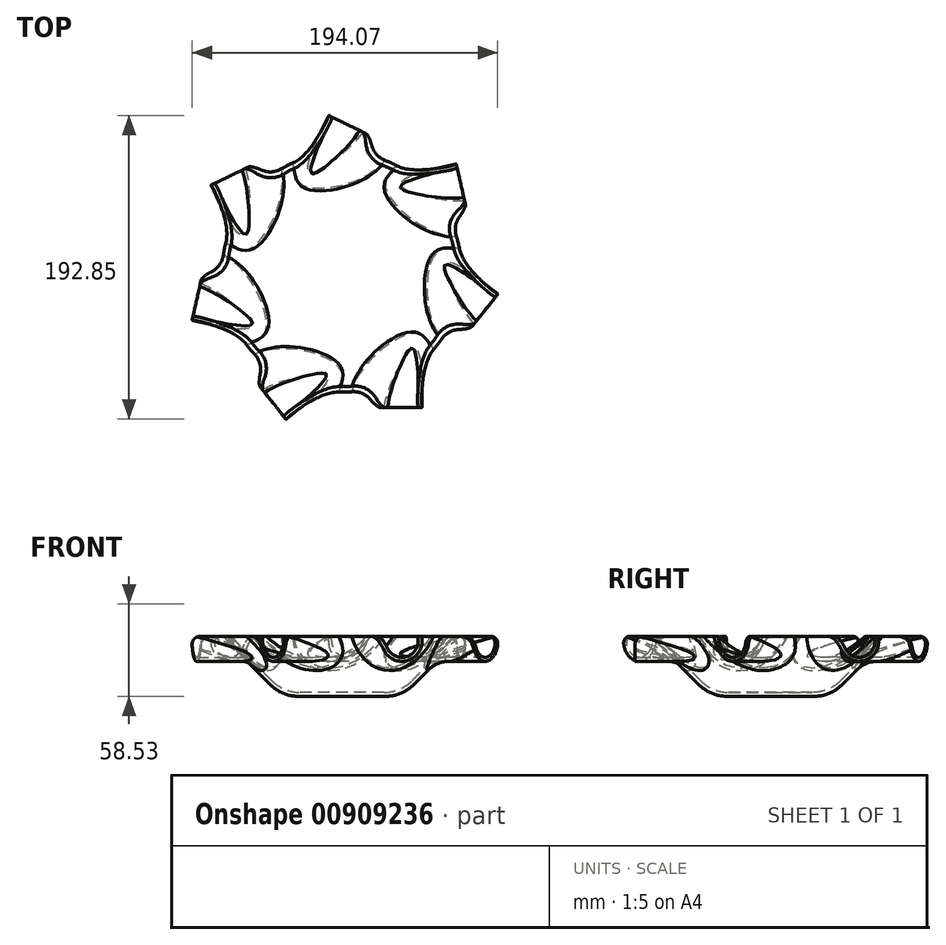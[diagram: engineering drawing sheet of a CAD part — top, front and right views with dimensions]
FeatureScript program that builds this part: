
annotation { "Feature Type Name" : "Feature", "Feature Type Description" : "" }
export const myFeature = defineFeature(function(context is Context, id is Id, definition is map)
    precondition{}
    {
        {
            var Q0;
            Q0=qCreatedBy(makeId("Front.planeOp"),FACE);
            var sketch = newSketch(context, id + "F0", { "sketchPlane" : qUnion([Q0])});
            skLineSegment(sketch, "E0", {"start": v(0, 0) * mm, "end": v(38.08, 0) * mm});
            skLineSegment(sketch, "E1", {"start": v(38.08, 0) * mm, "end": v(76.15, 38.08) * mm});
            skLineSegment(sketch, "E2", {"start": v(76.15, 38.08) * mm, "end": v(0, 38.08) * mm});
            skLineSegment(sketch, "E3", {"start": v(0, 38.08) * mm, "end": v(0, 0) * mm});
            skSolve(sketch);
        }
        {
            var Q0;
            Q0=makeQuery(id+"F0.imprint","IMPRINT",FACE,{"disambiguationData":[TD([[makeQuery(id+"F0.imprint","IMPRINT",EDGE,{"derivedFrom":sQuery(id+"F0.wireOp",EDGE,"E0")}),1.0]])]});
            var Q1;
            Q1=sQuery(id+"F0.wireOp",EDGE,"E3");
            revolve(context, id + "F1", {"surfaceOperationType" : NewSurfaceOperationType.NEW, "entities" : qUnion([Q0]), "axis" : qUnion([Q1]), "revolveType" : RevolveType.FULL});
        }
        {
            var Q0;
            Q0=qCreatedBy(makeId("Front.planeOp"),FACE);
            var sketch = newSketch(context, id + "F2", { "sketchPlane" : qUnion([Q0])});
            skLineSegment(sketch, "E4.0", {"start": v(-76.15, 38.08) * mm, "end": v(76.15, 38.08) * mm});
            skLineSegment(sketch, "E5", {"start": v(76.15, 38.08) * mm, "end": v(38.08, 0) * mm});
            skLineSegment(sketch, "E6", {"start": v(-38.08, 0) * mm, "end": v(-76.15, 38.08) * mm});
            skLineSegment(sketch, "E7.0", {"start": v(-38.08, 0) * mm, "end": v(38.08, 0) * mm});
            skCircle(sketch, "E8", {"center": v(38.08, 35) * mm, "radius": 12.76 * mm});
            skSolve(sketch);
        }
        {
            var Q0;
            {var subQ0=sQuery(id+"F2.wireOp",EDGE,"E8");var subQ1=sQuery(id+"F2.wireOp",EDGE,"E4.0");var subQ2=makeQuery(id+"F2.imprint","INTERSECT",VERTEX,{"disambiguationData":[OD(0.0)],"derivedFrom":[subQ1,subQ0]});Q0=makeQuery(id+"F2.imprint","IMPRINT",FACE,{"disambiguationData":[TD([[makeQuery(id+"F2.imprint","IMPRINT",EDGE,{"disambiguationData":[TD([[subQ2,-1.0]])],"derivedFrom":subQ1}),-1.0]])]});}
            extrude(context, id + "F3", {"entities" : qUnion([Q0]), "depth" : 86.04 * mm, "offsetDistance" : 25 * mm});
        }
        {
            var Q0;
            Q0=makeQuery(id+"F3.opExtrude","SWEPT_BODY",BODY,{"disambiguationData":[OSD([sQuery(id+"F2.wireOp",EDGE,"E4.0"),sQuery(id+"F2.wireOp",EDGE,"E8")])]});
            var Q1;
            Q1=makeQuery(id+"F1.opRevolve","SWEPT_FACE",FACE,{"disambiguationData":[OSD([sQuery(id+"F0.wireOp",EDGE,"E1")])]});
            circularPattern(context, id + "F4", {"operationType" : NewBodyOperationType.ADD, "entities" : qUnion([Q0]), "axis" : qUnion([Q1]), "angle" : 360 * degree, "instanceCount" : 7, "equalSpace" : true});
        }
        {
            var Q0;
            Q0=makeQuery(id+"F4.boolean.opBoolean","INTERSECT",EDGE,{"derivedFrom":[makeQuery(id+"F1.opRevolve","SWEPT_FACE",FACE,{"disambiguationData":[OSD([sQuery(id+"F0.wireOp",EDGE,"E1")])]}),makeQuery(id+"F4.opPattern","COPY",FACE,{"derivedFrom":makeQuery(id+"F3.opExtrude","SWEPT_FACE",FACE,{"disambiguationData":[OSD([sQuery(id+"F2.wireOp",EDGE,"E8")])]}),"instanceName":"6"})]});
            var Q1;
            Q1=makeQuery(id+"F4.boolean.opBoolean","INTERSECT",EDGE,{"derivedFrom":[makeQuery(id+"F1.opRevolve","SWEPT_FACE",FACE,{"disambiguationData":[OSD([sQuery(id+"F0.wireOp",EDGE,"E1")])]}),makeQuery(id+"F3.opExtrude","SWEPT_FACE",FACE,{"disambiguationData":[OSD([sQuery(id+"F2.wireOp",EDGE,"E8")])]})]});
            var Q2;
            Q2=makeQuery(id+"F4.boolean.opBoolean","INTERSECT",EDGE,{"derivedFrom":[makeQuery(id+"F1.opRevolve","SWEPT_FACE",FACE,{"disambiguationData":[OSD([sQuery(id+"F0.wireOp",EDGE,"E1")])]}),makeQuery(id+"F4.opPattern","COPY",FACE,{"derivedFrom":makeQuery(id+"F3.opExtrude","SWEPT_FACE",FACE,{"disambiguationData":[OSD([sQuery(id+"F2.wireOp",EDGE,"E8")])]}),"instanceName":"1"})]});
            var Q3;
            Q3=makeQuery(id+"F4.boolean.opBoolean","INTERSECT",EDGE,{"derivedFrom":[makeQuery(id+"F1.opRevolve","SWEPT_FACE",FACE,{"disambiguationData":[OSD([sQuery(id+"F0.wireOp",EDGE,"E1")])]}),makeQuery(id+"F4.opPattern","COPY",FACE,{"derivedFrom":makeQuery(id+"F3.opExtrude","SWEPT_FACE",FACE,{"disambiguationData":[OSD([sQuery(id+"F2.wireOp",EDGE,"E8")])]}),"instanceName":"5"})]});
            var Q4;
            Q4=makeQuery(id+"F4.boolean.opBoolean","INTERSECT",EDGE,{"derivedFrom":[makeQuery(id+"F1.opRevolve","SWEPT_FACE",FACE,{"disambiguationData":[OSD([sQuery(id+"F0.wireOp",EDGE,"E1")])]}),makeQuery(id+"F4.opPattern","COPY",FACE,{"derivedFrom":makeQuery(id+"F3.opExtrude","SWEPT_FACE",FACE,{"disambiguationData":[OSD([sQuery(id+"F2.wireOp",EDGE,"E8")])]}),"instanceName":"4"})]});
            var Q5;
            Q5=makeQuery(id+"F4.boolean.opBoolean","INTERSECT",EDGE,{"derivedFrom":[makeQuery(id+"F1.opRevolve","SWEPT_FACE",FACE,{"disambiguationData":[OSD([sQuery(id+"F0.wireOp",EDGE,"E1")])]}),makeQuery(id+"F4.opPattern","COPY",FACE,{"derivedFrom":makeQuery(id+"F3.opExtrude","SWEPT_FACE",FACE,{"disambiguationData":[OSD([sQuery(id+"F2.wireOp",EDGE,"E8")])]}),"instanceName":"3"})]});
            var Q6;
            Q6=makeQuery(id+"F4.boolean.opBoolean","INTERSECT",EDGE,{"derivedFrom":[makeQuery(id+"F1.opRevolve","SWEPT_FACE",FACE,{"disambiguationData":[OSD([sQuery(id+"F0.wireOp",EDGE,"E1")])]}),makeQuery(id+"F4.opPattern","COPY",FACE,{"derivedFrom":makeQuery(id+"F3.opExtrude","SWEPT_FACE",FACE,{"disambiguationData":[OSD([sQuery(id+"F2.wireOp",EDGE,"E8")])]}),"instanceName":"2"})]});
            fillet(context, id + "F5", {"entities" : qUnion([Q0, Q1, Q2, Q3, Q4, Q5, Q6]), "radius" : 20 * mm, "tangentPropagation" : true, "allowEdgeOverflow" : false});
        }
        {
            var Q0;
            {var subQ0=makeQuery(id+"F3.opExtrude","SWEPT_FACE",FACE,{"disambiguationData":[OSD([sQuery(id+"F2.wireOp",EDGE,"E4.0")])]});Q0=makeQuery(id+"F4.boolean.opBoolean","MERGE",FACE,{"derivedFrom":[makeQuery(id+"F1.opRevolve","SWEPT_FACE",FACE,{"disambiguationData":[OSD([sQuery(id+"F0.wireOp",EDGE,"E2")])]}),subQ0,makeQuery(id+"F4.opPattern","COPY",FACE,{"derivedFrom":subQ0,"instanceName":"1"}),makeQuery(id+"F4.opPattern","COPY",FACE,{"derivedFrom":subQ0,"instanceName":"2"}),makeQuery(id+"F4.opPattern","COPY",FACE,{"derivedFrom":subQ0,"instanceName":"3"}),makeQuery(id+"F4.opPattern","COPY",FACE,{"derivedFrom":subQ0,"instanceName":"4"}),makeQuery(id+"F4.opPattern","COPY",FACE,{"derivedFrom":subQ0,"instanceName":"5"}),makeQuery(id+"F4.opPattern","COPY",FACE,{"derivedFrom":subQ0,"instanceName":"6"})]});}
            var Q1;
            Q1=makeQuery(id+"F4.opPattern","COPY",FACE,{"derivedFrom":makeQuery(id+"F3.opExtrude","CAP_FACE",FACE,{"disambiguationData":[OSD([sQuery(id+"F2.wireOp",EDGE,"E4.0"),sQuery(id+"F2.wireOp",EDGE,"E8")])],"isStart":false}),"instanceName":"5"});
            var Q2;
            Q2=makeQuery(id+"F3.opExtrude","CAP_FACE",FACE,{"disambiguationData":[OSD([sQuery(id+"F2.wireOp",EDGE,"E4.0"),sQuery(id+"F2.wireOp",EDGE,"E8")])],"isStart":false});
            var Q3;
            Q3=makeQuery(id+"F4.opPattern","COPY",FACE,{"derivedFrom":makeQuery(id+"F3.opExtrude","CAP_FACE",FACE,{"disambiguationData":[OSD([sQuery(id+"F2.wireOp",EDGE,"E4.0"),sQuery(id+"F2.wireOp",EDGE,"E8")])],"isStart":false}),"instanceName":"6"});
            var Q4;
            Q4=makeQuery(id+"F4.opPattern","COPY",FACE,{"derivedFrom":makeQuery(id+"F3.opExtrude","CAP_FACE",FACE,{"disambiguationData":[OSD([sQuery(id+"F2.wireOp",EDGE,"E4.0"),sQuery(id+"F2.wireOp",EDGE,"E8")])],"isStart":false}),"instanceName":"1"});
            var Q5;
            Q5=makeQuery(id+"F4.opPattern","COPY",FACE,{"derivedFrom":makeQuery(id+"F3.opExtrude","CAP_FACE",FACE,{"disambiguationData":[OSD([sQuery(id+"F2.wireOp",EDGE,"E4.0"),sQuery(id+"F2.wireOp",EDGE,"E8")])],"isStart":false}),"instanceName":"2"});
            var Q6;
            Q6=makeQuery(id+"F4.opPattern","COPY",FACE,{"derivedFrom":makeQuery(id+"F3.opExtrude","CAP_FACE",FACE,{"disambiguationData":[OSD([sQuery(id+"F2.wireOp",EDGE,"E4.0"),sQuery(id+"F2.wireOp",EDGE,"E8")])],"isStart":false}),"instanceName":"3"});
            var Q7;
            Q7=makeQuery(id+"F4.opPattern","COPY",FACE,{"derivedFrom":makeQuery(id+"F3.opExtrude","CAP_FACE",FACE,{"disambiguationData":[OSD([sQuery(id+"F2.wireOp",EDGE,"E4.0"),sQuery(id+"F2.wireOp",EDGE,"E8")])],"isStart":false}),"instanceName":"4"});
            shell(context, id + "F6", {"entities" : qUnion([Q0, Q1, Q2, Q3, Q4, Q5, Q6, Q7]), "thickness" : 2.5 * mm});
        }
        {
            var Q0;
            Q0=makeQuery(id+"F6.opShell","OFFSET_EDGE",EDGE,{"disambiguationData":[OSD([sQuery(id+"F0.wireOp",EDGE,"E0"),sQuery(id+"F0.wireOp",EDGE,"E1")])]});
            var Q1;
            Q1=makeQuery(id+"F1.opRevolve","SWEPT_FACE",FACE,{"disambiguationData":[OSD([sQuery(id+"F0.wireOp",EDGE,"E0")])]});
            fillet(context, id + "F7", {"entities" : qUnion([Q0, Q1]), "radius" : 25 * mm, "tangentPropagation" : true, "allowEdgeOverflow" : false});
        }
        {
            var Q0;
            {var subQ0=sQuery(id+"F2.wireOp",EDGE,"E4.0");Q0=makeQuery(id+"F6.opShell","OFFSET_EDGE",EDGE,{"disambiguationData":[OSD([subQ0]),TDD([makeQuery(id+"F4.opPattern","COPY",EDGE,{"derivedFrom":makeQuery(id+"F3.opExtrude","CAP_EDGE",EDGE,{"disambiguationData":[OSD([subQ0])],"isStart":false}),"instanceName":"2"})])]});}
            var Q1;
            Q1=makeQuery(id+"F4.opPattern","COPY",EDGE,{"derivedFrom":makeQuery(id+"F3.opExtrude","CAP_EDGE",EDGE,{"disambiguationData":[OSD([sQuery(id+"F2.wireOp",EDGE,"E4.0")])],"isStart":false}),"instanceName":"2"});
            var Q2;
            {var subQ0=sQuery(id+"F2.wireOp",EDGE,"E4.0");Q2=makeQuery(id+"F6.opShell","OFFSET_EDGE",EDGE,{"disambiguationData":[OSD([subQ0]),TDD([makeQuery(id+"F4.opPattern","COPY",EDGE,{"derivedFrom":makeQuery(id+"F3.opExtrude","CAP_EDGE",EDGE,{"disambiguationData":[OSD([subQ0])],"isStart":false}),"instanceName":"1"})])]});}
            var Q3;
            Q3=makeQuery(id+"F4.opPattern","COPY",EDGE,{"derivedFrom":makeQuery(id+"F3.opExtrude","CAP_EDGE",EDGE,{"disambiguationData":[OSD([sQuery(id+"F2.wireOp",EDGE,"E4.0")])],"isStart":false}),"instanceName":"1"});
            var Q4;
            {var subQ0=sQuery(id+"F2.wireOp",EDGE,"E4.0");Q4=makeQuery(id+"F6.opShell","OFFSET_EDGE",EDGE,{"disambiguationData":[OSD([subQ0]),TDD([makeQuery(id+"F3.opExtrude","CAP_EDGE",EDGE,{"disambiguationData":[OSD([subQ0])],"isStart":false})])]});}
            var Q5;
            Q5=makeQuery(id+"F3.opExtrude","CAP_EDGE",EDGE,{"disambiguationData":[OSD([sQuery(id+"F2.wireOp",EDGE,"E4.0")])],"isStart":false});
            var Q6;
            {var subQ0=sQuery(id+"F2.wireOp",EDGE,"E4.0");Q6=makeQuery(id+"F6.opShell","OFFSET_EDGE",EDGE,{"disambiguationData":[OSD([subQ0]),TDD([makeQuery(id+"F4.opPattern","COPY",EDGE,{"derivedFrom":makeQuery(id+"F3.opExtrude","CAP_EDGE",EDGE,{"disambiguationData":[OSD([subQ0])],"isStart":false}),"instanceName":"6"})])]});}
            var Q7;
            Q7=makeQuery(id+"F4.opPattern","COPY",EDGE,{"derivedFrom":makeQuery(id+"F3.opExtrude","CAP_EDGE",EDGE,{"disambiguationData":[OSD([sQuery(id+"F2.wireOp",EDGE,"E4.0")])],"isStart":false}),"instanceName":"6"});
            var Q8;
            {var subQ0=sQuery(id+"F2.wireOp",EDGE,"E4.0");Q8=makeQuery(id+"F6.opShell","OFFSET_EDGE",EDGE,{"disambiguationData":[OSD([subQ0]),TDD([makeQuery(id+"F4.opPattern","COPY",EDGE,{"derivedFrom":makeQuery(id+"F3.opExtrude","CAP_EDGE",EDGE,{"disambiguationData":[OSD([subQ0])],"isStart":false}),"instanceName":"5"})])]});}
            var Q9;
            Q9=makeQuery(id+"F4.opPattern","COPY",EDGE,{"derivedFrom":makeQuery(id+"F3.opExtrude","CAP_EDGE",EDGE,{"disambiguationData":[OSD([sQuery(id+"F2.wireOp",EDGE,"E4.0")])],"isStart":false}),"instanceName":"5"});
            var Q10;
            {var subQ0=sQuery(id+"F2.wireOp",EDGE,"E4.0");Q10=makeQuery(id+"F6.opShell","OFFSET_EDGE",EDGE,{"disambiguationData":[OSD([subQ0]),TDD([makeQuery(id+"F4.opPattern","COPY",EDGE,{"derivedFrom":makeQuery(id+"F3.opExtrude","CAP_EDGE",EDGE,{"disambiguationData":[OSD([subQ0])],"isStart":false}),"instanceName":"4"})])]});}
            var Q11;
            Q11=makeQuery(id+"F4.opPattern","COPY",EDGE,{"derivedFrom":makeQuery(id+"F3.opExtrude","CAP_EDGE",EDGE,{"disambiguationData":[OSD([sQuery(id+"F2.wireOp",EDGE,"E4.0")])],"isStart":false}),"instanceName":"4"});
            var Q12;
            {var subQ0=sQuery(id+"F2.wireOp",EDGE,"E4.0");Q12=makeQuery(id+"F6.opShell","OFFSET_EDGE",EDGE,{"disambiguationData":[OSD([subQ0]),TDD([makeQuery(id+"F4.opPattern","COPY",EDGE,{"derivedFrom":makeQuery(id+"F3.opExtrude","CAP_EDGE",EDGE,{"disambiguationData":[OSD([subQ0])],"isStart":false}),"instanceName":"3"})])]});}
            var Q13;
            Q13=makeQuery(id+"F4.opPattern","COPY",EDGE,{"derivedFrom":makeQuery(id+"F3.opExtrude","CAP_EDGE",EDGE,{"disambiguationData":[OSD([sQuery(id+"F2.wireOp",EDGE,"E4.0")])],"isStart":false}),"instanceName":"3"});
            fillet(context, id + "F8", {"entities" : qUnion([Q0, Q1, Q2, Q3, Q4, Q5, Q6, Q7, Q8, Q9, Q10, Q11, Q12, Q13]), "radius" : 5 * mm, "tangentPropagation" : true, "allowEdgeOverflow" : false});
        }
    });
